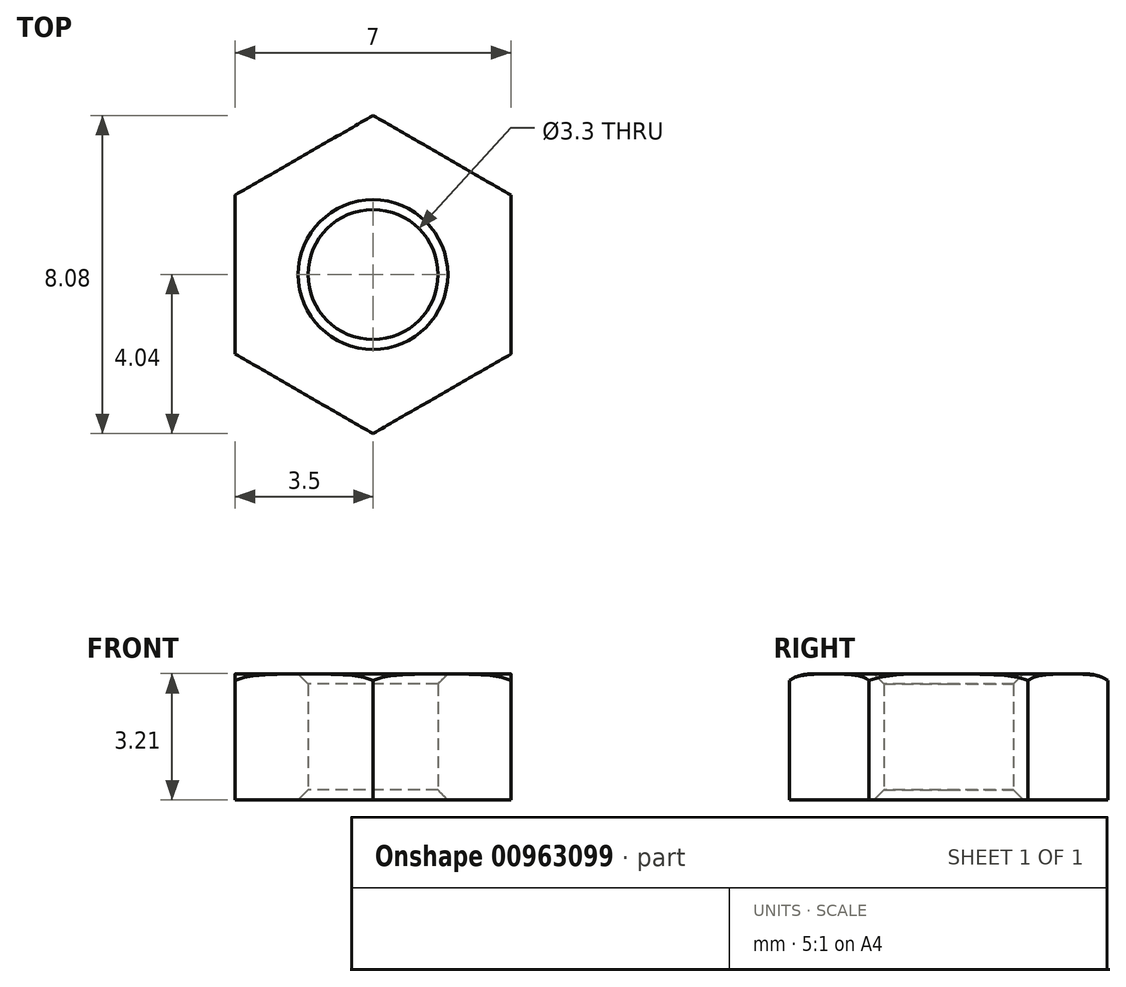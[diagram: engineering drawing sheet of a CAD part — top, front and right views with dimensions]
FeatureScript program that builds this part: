
annotation { "Feature Type Name" : "Feature", "Feature Type Description" : "" }
export const myFeature = defineFeature(function(context is Context, id is Id, definition is map)
    precondition{}
    {
        {
            var Q0;
            Q0=qCreatedBy(makeId("Top.planeOp"),FACE);
            var sketch = newSketch(context, id + "F0", { "sketchPlane" : qUnion([Q0])});
            skCircle(sketch, "E0.cCircle", {"center": v(0, 0) * mm, "radius": 3.5 * mm, "construction": true});
            skLineSegment(sketch, "E0.0", {"start": v(0, 4.04) * mm, "end": v(3.5, 2.02) * mm});
            skLineSegment(sketch, "E0.1", {"start": v(3.5, 2.02) * mm, "end": v(3.5, -2.02) * mm});
            skLineSegment(sketch, "E0.2", {"start": v(3.5, -2.02) * mm, "end": v(0, -4.04) * mm});
            skLineSegment(sketch, "E0.3", {"start": v(0, -4.04) * mm, "end": v(-3.5, -2.02) * mm});
            skLineSegment(sketch, "E0.4", {"start": v(-3.5, -2.02) * mm, "end": v(-3.5, 2.02) * mm});
            skLineSegment(sketch, "E0.5", {"start": v(-3.5, 2.02) * mm, "end": v(0, 4.04) * mm});
            skPoint(sketch, "E0.0.midPoint", {"position": v(1.75, 3.03) * mm});
            skCircle(sketch, "E1", {"center": v(0, 0) * mm, "radius": 1.65 * mm});
            skSolve(sketch);
        }
        {
            var Q0;
            Q0=qSketchRegion(id+"F0",true);
            extrude(context, id + "F1", {"entities" : qUnion([Q0]), "depth" : 3.2 * mm, "offsetDistance" : 25 * mm, "symmetric" : true});
        }
        {
            var Q0;
            Q0=qCreatedBy(makeId("Front.planeOp"),FACE);
            var sketch = newSketch(context, id + "F2", { "sketchPlane" : qUnion([Q0])});
            skArc(sketch, "E2", {"start": v(4.4, 1.04) * mm, "mid": v(4.03, 1.45) * mm, "end": v(3.5, 1.6) * mm});
            skLineSegment(sketch, "E3", {"start": v(3.5, 1.6) * mm, "end": v(4.4, 1.6) * mm});
            skLineSegment(sketch, "E4", {"start": v(4.4, 1.6) * mm, "end": v(4.4, 1.04) * mm});
            skSolve(sketch);
        }
        {
            var Q0;
            Q0=qSketchRegion(id+"F2",true);
            var Q1;
            Q1=makeQuery(id+"F1.opExtrude","SWEPT_FACE",FACE,{"disambiguationData":[OSD([sQuery(id+"F0.wireOp",EDGE,"E1")])]});
            revolve(context, id + "F3", {"operationType" : NewBodyOperationType.REMOVE, "surfaceOperationType" : NewSurfaceOperationType.NEW, "entities" : qUnion([Q0]), "axis" : qUnion([Q1]), "revolveType" : RevolveType.FULL, "oppositeDirection" : true});
        }
        {
            var Q0;
            Q0=makeQuery(id+"F1.opExtrude","SWEPT_FACE",FACE,{"disambiguationData":[OSD([sQuery(id+"F0.wireOp",EDGE,"E1")])]});
            chamfer(context, id + "F4", {"entities" : qUnion([Q0]), "width" : 0.25 * mm, "tangentPropagation" : true});
        }
    });
